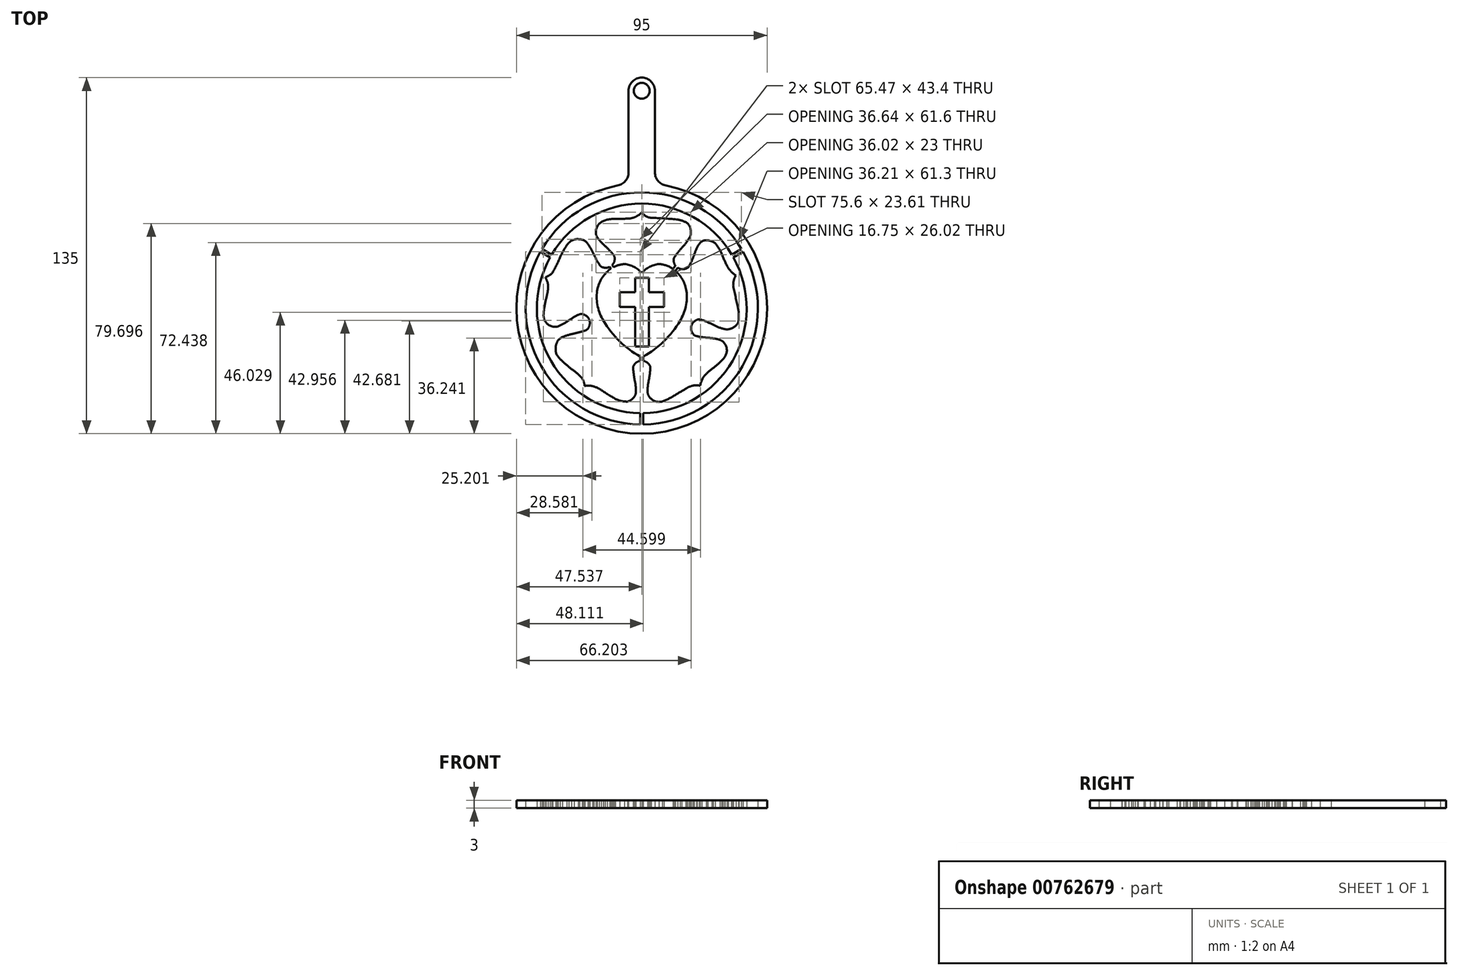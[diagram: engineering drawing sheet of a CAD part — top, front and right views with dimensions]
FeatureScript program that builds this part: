
annotation { "Feature Type Name" : "Feature", "Feature Type Description" : "" }
export const myFeature = defineFeature(function(context is Context, id is Id, definition is map)
    precondition{}
    {
        {
            var Q0;
            Q0=qCreatedBy(makeId("Top.planeOp"),FACE);
            var sketch = newSketch(context, id + "F0", { "sketchPlane" : qUnion([Q0])});
            skLineSegment(sketch, "E0.bottom", {"start": v(-45, 45) * mm, "end": v(45, 45) * mm});
            skLineSegment(sketch, "E0.top", {"start": v(-45, -45) * mm, "end": v(45, -45) * mm});
            skLineSegment(sketch, "E0.left", {"start": v(-45, 45) * mm, "end": v(-45, -45) * mm});
            skLineSegment(sketch, "E0.right", {"start": v(45, 45) * mm, "end": v(45, -45) * mm});
            skCircle(sketch, "E1", {"center": v(0, 0) * mm, "radius": 44 * mm});
            skCircle(sketch, "E2", {"center": v(0, 0) * mm, "radius": 39.75 * mm});
            skLineSegment(sketch, "E3.bottom", {"start": v(-2.5, 11.54) * mm, "end": v(2.7, 11.54) * mm});
            skLineSegment(sketch, "E3.top", {"start": v(-2.5, -14.48) * mm, "end": v(2.7, -14.48) * mm});
            skLineSegment(sketch, "E3.left", {"start": v(-2.5, 11.54) * mm, "end": v(-2.5, -14.48) * mm});
            skLineSegment(sketch, "E3.right", {"start": v(2.7, 11.54) * mm, "end": v(2.7, -14.48) * mm});
            skLineSegment(sketch, "E4.bottom", {"start": v(-8.34, 6.12) * mm, "end": v(8.41, 6.12) * mm});
            skLineSegment(sketch, "E4.top", {"start": v(-8.34, 0.57) * mm, "end": v(8.41, 0.57) * mm});
            skLineSegment(sketch, "E4.left", {"start": v(-8.34, 6.12) * mm, "end": v(-8.34, 0.57) * mm});
            skLineSegment(sketch, "E4.right", {"start": v(8.41, 6.12) * mm, "end": v(8.41, 0.57) * mm});
            skArc(sketch, "E5", {"start": v(6.54, 16.79) * mm, "mid": v(2.95, 15.73) * mm, "end": v(0, 13.44) * mm});
            skArc(sketch, "E6", {"start": v(12, 14.86) * mm, "mid": v(9.4, 16.22) * mm, "end": v(6.54, 16.79) * mm});
            skArc(sketch, "E7", {"start": v(16.95, 6.56) * mm, "mid": v(15.27, 11.18) * mm, "end": v(12, 14.86) * mm});
            skArc(sketch, "E8", {"start": v(14.48, -4.74) * mm, "mid": v(16.7, 0.7) * mm, "end": v(16.95, 6.56) * mm});
            skArc(sketch, "E9", {"start": v(0, -18.58) * mm, "mid": v(8.19, -12.65) * mm, "end": v(14.48, -4.74) * mm});
            skLineSegment(sketch, "E10", {"start": v(0, 13.44) * mm, "end": v(0, -18.58) * mm});
            skArc(sketch, "E11.MirrorCS", {"start": v(-6.54, 16.79) * mm, "mid": v(-2.95, 15.73) * mm, "end": v(0, 13.44) * mm});
            skArc(sketch, "E12.MirrorCS", {"start": v(-12, 14.86) * mm, "mid": v(-9.4, 16.22) * mm, "end": v(-6.54, 16.79) * mm});
            skArc(sketch, "E13.MirrorCS", {"start": v(-16.95, 6.56) * mm, "mid": v(-15.27, 11.18) * mm, "end": v(-12, 14.86) * mm});
            skArc(sketch, "E14.MirrorCS", {"start": v(-14.48, -4.74) * mm, "mid": v(-16.7, 0.7) * mm, "end": v(-16.95, 6.56) * mm});
            skArc(sketch, "E15.MirrorCS", {"start": v(0, -18.58) * mm, "mid": v(-8.19, -12.65) * mm, "end": v(-14.48, -4.74) * mm});
            skArc(sketch, "E16", {"start": v(0, 36.44) * mm, "mid": v(1.55, 35) * mm, "end": v(3.57, 34.33) * mm});
            skArc(sketch, "E17", {"start": v(13.22, 33.72) * mm, "mid": v(8.4, 34.11) * mm, "end": v(3.57, 34.33) * mm});
            skArc(sketch, "E18", {"start": v(18.08, 31.78) * mm, "mid": v(15.79, 33.1) * mm, "end": v(13.22, 33.72) * mm});
            skArc(sketch, "E19", {"start": v(19.53, 28.72) * mm, "mid": v(19.07, 30.38) * mm, "end": v(18.08, 31.78) * mm});
            skArc(sketch, "E20", {"start": v(17.86, 25.1) * mm, "mid": v(18.99, 26.77) * mm, "end": v(19.53, 28.72) * mm});
            skLineSegment(sketch, "E21", {"start": v(17.86, 25.1) * mm, "end": v(15.52, 22.1) * mm});
            skArc(sketch, "E22", {"start": v(15.52, 22.1) * mm, "mid": v(14.15, 20.52) * mm, "end": v(13.15, 18.7) * mm});
            skArc(sketch, "E23", {"start": v(13.15, 18.7) * mm, "mid": v(14.32, 15.74) * mm, "end": v(17.36, 16.66) * mm});
            skArc(sketch, "E24", {"start": v(17.36, 16.66) * mm, "mid": v(18.3, 18.64) * mm, "end": v(19.06, 20.7) * mm});
            skArc(sketch, "E25", {"start": v(20.46, 24.12) * mm, "mid": v(19.7, 22.44) * mm, "end": v(19.06, 20.7) * mm});
            skArc(sketch, "E26", {"start": v(23.5, 26.42) * mm, "mid": v(21.72, 25.62) * mm, "end": v(20.46, 24.12) * mm});
            skArc(sketch, "E27", {"start": v(27.15, 25.4) * mm, "mid": v(25.46, 26.38) * mm, "end": v(23.5, 26.42) * mm});
            skArc(sketch, "E28", {"start": v(30.36, 20.5) * mm, "mid": v(29, 23.12) * mm, "end": v(27.15, 25.4) * mm});
            skArc(sketch, "E29", {"start": v(30.36, 20.5) * mm, "mid": v(31.52, 17.83) * mm, "end": v(32.79, 15.22) * mm});
            skArc(sketch, "E30", {"start": v(32.79, 15.22) * mm, "mid": v(34.12, 13.72) * mm, "end": v(35.67, 12.44) * mm});
            skArc(sketch, "E31", {"start": v(35.67, 12.44) * mm, "mid": v(34.86, 10.6) * mm, "end": v(34.66, 8.59) * mm});
            skArc(sketch, "E32", {"start": v(34.66, 8.59) * mm, "mid": v(35.54, 4.4) * mm, "end": v(36.48, 0.21) * mm});
            skArc(sketch, "E33", {"start": v(36.56, -5.45) * mm, "mid": v(36.8, -2.62) * mm, "end": v(36.48, 0.21) * mm});
            skArc(sketch, "E34", {"start": v(34.01, -8.4) * mm, "mid": v(35.55, -7.15) * mm, "end": v(36.56, -5.45) * mm});
            skArc(sketch, "E35", {"start": v(31.16, -8.48) * mm, "mid": v(32.6, -8.67) * mm, "end": v(34.01, -8.4) * mm});
            skArc(sketch, "E36", {"start": v(24.37, -5.6) * mm, "mid": v(27.72, -7.16) * mm, "end": v(31.16, -8.48) * mm});
            skArc(sketch, "E37", {"start": v(24.37, -5.6) * mm, "mid": v(22.92, -5.17) * mm, "end": v(21.4, -5.26) * mm});
            skArc(sketch, "E38", {"start": v(21.4, -5.26) * mm, "mid": v(20.45, -5.78) * mm, "end": v(19.83, -6.68) * mm});
            skArc(sketch, "E39", {"start": v(19.83, -6.68) * mm, "mid": v(19.7, -7.91) * mm, "end": v(20.32, -8.98) * mm});
            skArc(sketch, "E40", {"start": v(20.32, -8.98) * mm, "mid": v(21.64, -9.79) * mm, "end": v(23.15, -10.1) * mm});
            skArc(sketch, "E41", {"start": v(26.9, -10.46) * mm, "mid": v(25.03, -10.25) * mm, "end": v(23.15, -10.1) * mm});
            skArc(sketch, "E42", {"start": v(30.56, -11.14) * mm, "mid": v(28.76, -10.62) * mm, "end": v(26.9, -10.46) * mm});
            skArc(sketch, "E43", {"start": v(32.8, -13.84) * mm, "mid": v(31.94, -12.28) * mm, "end": v(30.56, -11.14) * mm});
            skArc(sketch, "E44", {"start": v(32.36, -17.04) * mm, "mid": v(32.87, -15.44) * mm, "end": v(32.77, -13.76) * mm});
            skArc(sketch, "E45", {"start": v(30.2, -19.83) * mm, "mid": v(31.4, -18.53) * mm, "end": v(32.36, -17.04) * mm});
            skArc(sketch, "E46", {"start": v(27.09, -22.58) * mm, "mid": v(28.7, -21.26) * mm, "end": v(30.2, -19.83) * mm});
            skArc(sketch, "E47", {"start": v(27.09, -22.58) * mm, "mid": v(25.81, -23.54) * mm, "end": v(24.61, -24.6) * mm});
            skArc(sketch, "E48", {"start": v(24.61, -24.6) * mm, "mid": v(23.02, -26.68) * mm, "end": v(22.2, -29.16) * mm});
            skArc(sketch, "E49", {"start": v(22.2, -29.16) * mm, "mid": v(22.18, -29.26) * mm, "end": v(22.2, -29.36) * mm});
            skArc(sketch, "E50", {"start": v(22.2, -29.36) * mm, "mid": v(20.65, -29.14) * mm, "end": v(19.12, -29.35) * mm});
            skArc(sketch, "E51", {"start": v(19.12, -29.35) * mm, "mid": v(18.01, -29.75) * mm, "end": v(16.98, -30.3) * mm});
            skArc(sketch, "E52", {"start": v(12.71, -32.8) * mm, "mid": v(14.85, -31.56) * mm, "end": v(16.98, -30.3) * mm});
            skArc(sketch, "E53", {"start": v(7.81, -35.27) * mm, "mid": v(10.34, -34.18) * mm, "end": v(12.71, -32.8) * mm});
            skArc(sketch, "E54", {"start": v(1.9, -34.29) * mm, "mid": v(4.72, -35.62) * mm, "end": v(7.81, -35.27) * mm});
            skArc(sketch, "E55", {"start": v(1.07, -30.57) * mm, "mid": v(1.11, -32.52) * mm, "end": v(1.9, -34.29) * mm});
            skArc(sketch, "E56", {"start": v(1.9, -24.2) * mm, "mid": v(1.4, -27.38) * mm, "end": v(1.07, -30.57) * mm});
            skArc(sketch, "E57", {"start": v(1.9, -24.2) * mm, "mid": v(1.96, -22.8) * mm, "end": v(1.75, -21.4) * mm});
            skArc(sketch, "E58", {"start": v(1.75, -21.4) * mm, "mid": v(1.07, -20.51) * mm, "end": v(0, -20.16) * mm});
            skArc(sketch, "E59", {"start": v(0, -20.16) * mm, "mid": v(-1.25, -20.37) * mm, "end": v(-2.16, -21.26) * mm});
            skArc(sketch, "E60", {"start": v(-2.16, -21.26) * mm, "mid": v(-2.56, -22.74) * mm, "end": v(-2.48, -24.28) * mm});
            skArc(sketch, "E61", {"start": v(-1.5, -30.4) * mm, "mid": v(-1.92, -27.33) * mm, "end": v(-2.48, -24.28) * mm});
            skArc(sketch, "E62", {"start": v(-2.8, -34) * mm, "mid": v(-1.78, -32.33) * mm, "end": v(-1.5, -30.4) * mm});
            skArc(sketch, "E63", {"start": v(-5.21, -35.34) * mm, "mid": v(-3.87, -34.92) * mm, "end": v(-2.8, -34) * mm});
            skArc(sketch, "E64", {"start": v(-9.96, -34.34) * mm, "mid": v(-7.65, -35.14) * mm, "end": v(-5.21, -35.34) * mm});
            skArc(sketch, "E65", {"start": v(-15.27, -31.03) * mm, "mid": v(-12.64, -32.73) * mm, "end": v(-9.96, -34.34) * mm});
            skArc(sketch, "E66", {"start": v(-15.27, -31.03) * mm, "mid": v(-16.9, -30.09) * mm, "end": v(-18.68, -29.48) * mm});
            skArc(sketch, "E67", {"start": v(-18.68, -29.48) * mm, "mid": v(-20.16, -29.28) * mm, "end": v(-21.66, -29.42) * mm});
            skArc(sketch, "E68", {"start": v(-21.66, -29.42) * mm, "mid": v(-21.95, -27.92) * mm, "end": v(-22.6, -26.55) * mm});
            skArc(sketch, "E69", {"start": v(-22.6, -26.55) * mm, "mid": v(-24.45, -24.66) * mm, "end": v(-26.57, -23.08) * mm});
            skArc(sketch, "E70", {"start": v(-30, -20.12) * mm, "mid": v(-28.3, -21.62) * mm, "end": v(-26.57, -23.08) * mm});
            skArc(sketch, "E71", {"start": v(-33.13, -16.23) * mm, "mid": v(-31.72, -18.3) * mm, "end": v(-30, -20.12) * mm});
            skArc(sketch, "E72", {"start": v(-33.13, -12.1) * mm, "mid": v(-33.5, -14.16) * mm, "end": v(-33.13, -16.23) * mm});
            skArc(sketch, "E73", {"start": v(-30.28, -9.88) * mm, "mid": v(-31.94, -10.68) * mm, "end": v(-33.13, -12.1) * mm});
            skArc(sketch, "E74", {"start": v(-24.48, -8.35) * mm, "mid": v(-27.4, -9.06) * mm, "end": v(-30.28, -9.88) * mm});
            skArc(sketch, "E75", {"start": v(-24.48, -8.35) * mm, "mid": v(-22.88, -7.92) * mm, "end": v(-21.4, -7.18) * mm});
            skArc(sketch, "E76", {"start": v(-21.4, -7.18) * mm, "mid": v(-20.69, -6) * mm, "end": v(-20.79, -4.62) * mm});
            skArc(sketch, "E77", {"start": v(-20.79, -4.62) * mm, "mid": v(-21.7, -3.47) * mm, "end": v(-23.15, -3.15) * mm});
            skArc(sketch, "E78", {"start": v(-23.15, -3.15) * mm, "mid": v(-25.09, -3.75) * mm, "end": v(-26.83, -4.79) * mm});
            skArc(sketch, "E79", {"start": v(-30.09, -6.9) * mm, "mid": v(-28.44, -5.88) * mm, "end": v(-26.83, -4.79) * mm});
            skArc(sketch, "E80", {"start": v(-33.05, -7.75) * mm, "mid": v(-31.5, -7.58) * mm, "end": v(-30.09, -6.9) * mm});
            skArc(sketch, "E81", {"start": v(-36.25, -6.16) * mm, "mid": v(-34.83, -7.3) * mm, "end": v(-33.05, -7.75) * mm});
            skArc(sketch, "E82", {"start": v(-37.17, -1.77) * mm, "mid": v(-37.1, -4.05) * mm, "end": v(-36.25, -6.16) * mm});
            skArc(sketch, "E83", {"start": v(-36.28, 3.58) * mm, "mid": v(-36.83, 0.92) * mm, "end": v(-37.17, -1.77) * mm});
            skArc(sketch, "E84", {"start": v(-36.28, 3.58) * mm, "mid": v(-35.73, 5.9) * mm, "end": v(-35.5, 8.25) * mm});
            skArc(sketch, "E85", {"start": v(-35.5, 8.25) * mm, "mid": v(-35.77, 10.1) * mm, "end": v(-36.54, 11.8) * mm});
            skArc(sketch, "E86", {"start": v(-36.54, 11.8) * mm, "mid": v(-35.04, 12.53) * mm, "end": v(-33.78, 13.62) * mm});
            skArc(sketch, "E87", {"start": v(-33.78, 13.62) * mm, "mid": v(-32.25, 16.49) * mm, "end": v(-30.92, 19.46) * mm});
            skArc(sketch, "E88", {"start": v(-27.68, 25.02) * mm, "mid": v(-29.42, 22.3) * mm, "end": v(-30.92, 19.46) * mm});
            skArc(sketch, "E89", {"start": v(-23.95, 27.13) * mm, "mid": v(-26.01, 26.42) * mm, "end": v(-27.68, 25.02) * mm});
            skArc(sketch, "E90", {"start": v(-21.49, 26.75) * mm, "mid": v(-22.68, 27.16) * mm, "end": v(-23.95, 27.13) * mm});
            skArc(sketch, "E91", {"start": v(-19.35, 24.34) * mm, "mid": v(-20.3, 25.65) * mm, "end": v(-21.49, 26.75) * mm});
            skArc(sketch, "E92", {"start": v(-16.95, 19.97) * mm, "mid": v(-18.13, 22.17) * mm, "end": v(-19.35, 24.34) * mm});
            skArc(sketch, "E93", {"start": v(-16.95, 19.97) * mm, "mid": v(-16.12, 18.38) * mm, "end": v(-14.94, 17.03) * mm});
            skArc(sketch, "E94", {"start": v(-14.94, 17.03) * mm, "mid": v(-13.5, 16.52) * mm, "end": v(-12.08, 17.12) * mm});
            skArc(sketch, "E95", {"start": v(-12.08, 17.12) * mm, "mid": v(-11.4, 18.14) * mm, "end": v(-11.33, 19.36) * mm});
            skArc(sketch, "E96", {"start": v(-11.33, 19.36) * mm, "mid": v(-11.61, 20.08) * mm, "end": v(-12.02, 20.74) * mm});
            skArc(sketch, "E97", {"start": v(-12.02, 20.74) * mm, "mid": v(-13.03, 21.91) * mm, "end": v(-14.14, 22.98) * mm});
            skArc(sketch, "E98", {"start": v(-16.39, 24.95) * mm, "mid": v(-15.27, 23.96) * mm, "end": v(-14.14, 22.98) * mm});
            skArc(sketch, "E99", {"start": v(-18.17, 27.59) * mm, "mid": v(-17.42, 26.17) * mm, "end": v(-16.39, 24.95) * mm});
            skArc(sketch, "E100", {"start": v(-18.06, 30.68) * mm, "mid": v(-18.41, 29.15) * mm, "end": v(-18.17, 27.59) * mm});
            skArc(sketch, "E101", {"start": v(-15.51, 32.97) * mm, "mid": v(-17.01, 32.08) * mm, "end": v(-18.06, 30.68) * mm});
            skArc(sketch, "E102", {"start": v(-10.83, 33.93) * mm, "mid": v(-13.2, 33.62) * mm, "end": v(-15.51, 32.97) * mm});
            skArc(sketch, "E103", {"start": v(-10.83, 33.93) * mm, "mid": v(-8.11, 33.96) * mm, "end": v(-5.4, 34.03) * mm});
            skArc(sketch, "E104", {"start": v(-5.4, 34.03) * mm, "mid": v(-3.95, 34.19) * mm, "end": v(-2.56, 34.61) * mm});
            skArc(sketch, "E105", {"start": v(-2.56, 34.61) * mm, "mid": v(-1.17, 35.37) * mm, "end": v(0, 36.44) * mm});
            skCircle(sketch, "E106", {"center": v(0, 0) * mm, "radius": 47.5 * mm});
            skLineSegment(sketch, "E107", {"start": v(0.6, -44) * mm, "end": v(0.6, -39.75) * mm});
            skLineSegment(sketch, "E108.MirrorCS", {"start": v(-0.6, -44) * mm, "end": v(-0.6, -39.75) * mm});
            skLineSegment(sketch, "E109.1.0", {"start": v(38.4, 21.48) * mm, "end": v(34.72, 19.35) * mm});
            skLineSegment(sketch, "E109.1.1", {"start": v(37.8, 22.52) * mm, "end": v(34.12, 20.4) * mm});
            skLineSegment(sketch, "E109.2.0", {"start": v(-37.8, 22.52) * mm, "end": v(-34.12, 20.4) * mm});
            skLineSegment(sketch, "E109.2.1", {"start": v(-38.4, 21.48) * mm, "end": v(-34.72, 19.35) * mm});
            skLineSegment(sketch, "E110", {"start": v(0.6, -20.27) * mm, "end": v(0.6, -18.26) * mm});
            skLineSegment(sketch, "E111.MirrorCS", {"start": v(-0.6, -20.27) * mm, "end": v(-0.6, -18.26) * mm});
            skLineSegment(sketch, "E112.2.0", {"start": v(14.1, 15.86) * mm, "end": v(12.74, 14.25) * mm});
            skLineSegment(sketch, "E112.2.1", {"start": v(13.27, 16.75) * mm, "end": v(11.8, 15) * mm});
            skLineSegment(sketch, "E112.anchor1", {"start": v(0, 0) * mm, "end": v(-0.6, -20.27) * mm, "construction": true});
            skLineSegment(sketch, "E112.anchor2", {"start": v(0, 0) * mm, "end": v(13.49, 15.14) * mm, "construction": true});
            skLineSegment(sketch, "E113.2.0", {"start": v(-11.86, 17.34) * mm, "end": v(-10.66, 15.69) * mm});
            skLineSegment(sketch, "E113.2.1", {"start": v(-12.84, 16.65) * mm, "end": v(-11.7, 15.07) * mm});
            skLineSegment(sketch, "E113.anchor2", {"start": v(0, 0) * mm, "end": v(-11.43, 16.75) * mm, "construction": true});
            skPoint(sketch, "E114.orphan", {"position": v(-12.4, 16.05) * mm});
            skPoint(sketch, "E115.orphan", {"position": v(12.57, 15.91) * mm});
            skPoint(sketch, "E116.orphan", {"position": v(11.27, 14.37) * mm});
            skPoint(sketch, "E117.orphan", {"position": v(12.2, 13.6) * mm});
            skPoint(sketch, "E118.orphan", {"position": v(-11.22, 14.42) * mm});
            skPoint(sketch, "E119.orphan", {"position": v(-10.24, 15.12) * mm});
            skLineSegment(sketch, "E120.top", {"start": v(-5, 87.5) * mm, "end": v(5, 87.5) * mm});
            skLineSegment(sketch, "E120.left", {"start": v(-5, 47.24) * mm, "end": v(-5, 87.5) * mm});
            skLineSegment(sketch, "E120.right", {"start": v(5, 47.24) * mm, "end": v(5, 87.5) * mm});
            skArc(sketch, "E121", {"start": v(3.1, -33.84) * mm, "mid": v(5.23, -35.28) * mm, "end": v(7.81, -35.27) * mm});
            skArc(sketch, "E122", {"start": v(2.2, -31.7) * mm, "mid": v(2.47, -32.84) * mm, "end": v(3.1, -33.84) * mm});
            skArc(sketch, "E123", {"start": v(2.7, -27.1) * mm, "mid": v(2.3, -29.39) * mm, "end": v(2.2, -31.7) * mm});
            skArc(sketch, "E124", {"start": v(2.7, -27.1) * mm, "mid": v(3.03, -25.04) * mm, "end": v(3.24, -22.97) * mm});
            skArc(sketch, "E125", {"start": v(3.24, -22.97) * mm, "mid": v(3.16, -21.96) * mm, "end": v(2.63, -21.1) * mm});
            skArc(sketch, "E126.MirrorCS", {"start": v(-3.1, -33.84) * mm, "mid": v(-5.23, -35.28) * mm, "end": v(-7.81, -35.27) * mm});
            skArc(sketch, "E127.MirrorCS", {"start": v(-2.2, -31.7) * mm, "mid": v(-2.47, -32.84) * mm, "end": v(-3.1, -33.84) * mm});
            skArc(sketch, "E128.MirrorCS", {"start": v(-2.7, -27.1) * mm, "mid": v(-2.3, -29.39) * mm, "end": v(-2.2, -31.7) * mm});
            skArc(sketch, "E129.MirrorCS", {"start": v(-2.7, -27.1) * mm, "mid": v(-3.03, -25.04) * mm, "end": v(-3.24, -22.97) * mm});
            skArc(sketch, "E130.MirrorCS", {"start": v(-3.24, -22.97) * mm, "mid": v(-3.16, -21.96) * mm, "end": v(-2.63, -21.1) * mm});
            skArc(sketch, "E131", {"start": v(2.63, -21.1) * mm, "mid": v(0, -19.83) * mm, "end": v(-2.63, -21.1) * mm});
            skArc(sketch, "E132.1.1", {"start": v(26.54, -5.96) * mm, "mid": v(28.63, -6.97) * mm, "end": v(30.84, -7.7) * mm});
            skArc(sketch, "E132.1.2", {"start": v(26.54, -5.96) * mm, "mid": v(24.65, -5.09) * mm, "end": v(22.71, -4.32) * mm});
            skArc(sketch, "E132.1.3", {"start": v(22.71, -4.32) * mm, "mid": v(21.72, -4.13) * mm, "end": v(20.75, -4.4) * mm});
            skArc(sketch, "E132.1.4", {"start": v(20.75, -4.4) * mm, "mid": v(18.8, -6.59) * mm, "end": v(19.31, -9.47) * mm});
            skArc(sketch, "E132.1.5", {"start": v(20.95, -10.56) * mm, "mid": v(20, -10.2) * mm, "end": v(19.31, -9.47) * mm});
            skArc(sketch, "E132.1.6", {"start": v(25.06, -11.17) * mm, "mid": v(23, -10.92) * mm, "end": v(20.95, -10.56) * mm});
            skArc(sketch, "E132.1.7", {"start": v(25.06, -11.17) * mm, "mid": v(27.37, -11.41) * mm, "end": v(29.64, -11.94) * mm});
            skArc(sketch, "E132.1.8", {"start": v(29.64, -11.94) * mm, "mid": v(30.66, -12.51) * mm, "end": v(31.44, -13.38) * mm});
            skArc(sketch, "E132.1.9", {"start": v(31.44, -13.38) * mm, "mid": v(32.25, -15.83) * mm, "end": v(31.54, -18.31) * mm});
            skArc(sketch, "E132.2.1", {"start": v(15.15, 22.94) * mm, "mid": v(16.67, 24.7) * mm, "end": v(17.96, 26.62) * mm});
            skArc(sketch, "E132.2.2", {"start": v(15.15, 22.94) * mm, "mid": v(13.8, 21.34) * mm, "end": v(12.56, 19.67) * mm});
            skArc(sketch, "E132.2.3", {"start": v(12.56, 19.67) * mm, "mid": v(12.11, 18.77) * mm, "end": v(12.12, 17.76) * mm});
            skArc(sketch, "E132.2.4", {"start": v(12.12, 17.76) * mm, "mid": v(13.73, 15.31) * mm, "end": v(16.64, 15.05) * mm});
            skArc(sketch, "E132.2.5", {"start": v(18.12, 16.33) * mm, "mid": v(17.53, 15.51) * mm, "end": v(16.64, 15.05) * mm});
            skArc(sketch, "E132.2.6", {"start": v(19.79, 20.15) * mm, "mid": v(19, 18.22) * mm, "end": v(18.12, 16.33) * mm});
            skArc(sketch, "E132.2.7", {"start": v(19.79, 20.15) * mm, "mid": v(20.63, 22.31) * mm, "end": v(21.73, 24.36) * mm});
            skArc(sketch, "E132.3.1", {"start": v(-18.12, 20.33) * mm, "mid": v(-19.14, 22.42) * mm, "end": v(-20.41, 24.36) * mm});
            skArc(sketch, "E132.3.2", {"start": v(-18.12, 20.33) * mm, "mid": v(-17.17, 18.48) * mm, "end": v(-16.12, 16.68) * mm});
            skArc(sketch, "E132.3.3", {"start": v(-16.12, 16.68) * mm, "mid": v(-15.47, 15.9) * mm, "end": v(-14.53, 15.52) * mm});
            skArc(sketch, "E132.3.4", {"start": v(-14.53, 15.52) * mm, "mid": v(-11.66, 16.04) * mm, "end": v(-10.27, 18.62) * mm});
            skArc(sketch, "E132.3.5", {"start": v(-10.88, 20.49) * mm, "mid": v(-10.35, 19.63) * mm, "end": v(-10.27, 18.62) * mm});
            skArc(sketch, "E132.3.6", {"start": v(-13.74, 23.51) * mm, "mid": v(-12.26, 22.04) * mm, "end": v(-10.88, 20.49) * mm});
            skArc(sketch, "E132.3.7", {"start": v(-13.74, 23.51) * mm, "mid": v(-15.4, 25.13) * mm, "end": v(-16.86, 26.94) * mm});
            skArc(sketch, "E132.3.8", {"start": v(-16.86, 26.94) * mm, "mid": v(-17.3, 28.03) * mm, "end": v(-17.39, 29.2) * mm});
            skArc(sketch, "E132.3.9", {"start": v(-17.39, 29.2) * mm, "mid": v(-16.5, 31.62) * mm, "end": v(-14.41, 33.13) * mm});
            skArc(sketch, "E132.4.1", {"start": v(-25.57, -9.54) * mm, "mid": v(-27.83, -10.07) * mm, "end": v(-30.01, -10.87) * mm});
            skArc(sketch, "E132.4.2", {"start": v(-25.57, -9.54) * mm, "mid": v(-23.55, -9.04) * mm, "end": v(-21.56, -8.42) * mm});
            skArc(sketch, "E132.4.3", {"start": v(-21.56, -8.42) * mm, "mid": v(-20.66, -7.95) * mm, "end": v(-20.08, -7.13) * mm});
            skArc(sketch, "E132.4.4", {"start": v(-20.08, -7.13) * mm, "mid": v(-19.93, -4.21) * mm, "end": v(-22.13, -2.29) * mm});
            skArc(sketch, "E132.4.5", {"start": v(-24.1, -2.46) * mm, "mid": v(-23.13, -2.13) * mm, "end": v(-22.13, -2.29) * mm});
            skArc(sketch, "E132.4.6", {"start": v(-27.68, -4.56) * mm, "mid": v(-25.92, -3.46) * mm, "end": v(-24.1, -2.46) * mm});
            skArc(sketch, "E132.4.7", {"start": v(-27.68, -4.56) * mm, "mid": v(-29.63, -5.82) * mm, "end": v(-31.73, -6.83) * mm});
            skArc(sketch, "E132.4.8", {"start": v(-31.73, -6.83) * mm, "mid": v(-32.88, -7.02) * mm, "end": v(-34.04, -6.84) * mm});
            skArc(sketch, "E132.4.9", {"start": v(-34.04, -6.84) * mm, "mid": v(-36.2, -5.43) * mm, "end": v(-37.2, -3.05) * mm});
            skLineSegment(sketch, "E133", {"start": v(31.54, -18.31) * mm, "end": v(31.5, -18.41) * mm});
            skArc(sketch, "E134", {"start": v(30.84, -7.7) * mm, "mid": v(32.39, -7.94) * mm, "end": v(33.92, -7.63) * mm});
            skArc(sketch, "E135", {"start": v(33.92, -7.63) * mm, "mid": v(35.48, -6.7) * mm, "end": v(36.6, -5.27) * mm});
            skArc(sketch, "E136", {"start": v(17.96, 26.62) * mm, "mid": v(18.53, 27.82) * mm, "end": v(18.58, 29.14) * mm});
            skArc(sketch, "E137", {"start": v(18.58, 29.14) * mm, "mid": v(18.27, 30.87) * mm, "end": v(17.3, 32.33) * mm});
            skArc(sketch, "E138", {"start": v(24.37, 25.83) * mm, "mid": v(22.85, 25.45) * mm, "end": v(21.73, 24.36) * mm});
            skArc(sketch, "E139", {"start": v(27.88, 24.61) * mm, "mid": v(26.24, 25.54) * mm, "end": v(24.37, 25.83) * mm});
            skLineSegment(sketch, "E140", {"start": v(-14.41, 33.13) * mm, "end": v(-13.07, 33.64) * mm});
            skArc(sketch, "E141", {"start": v(-20.41, 24.36) * mm, "mid": v(-21.72, 25.7) * mm, "end": v(-23.52, 26.18) * mm});
            skArc(sketch, "E142", {"start": v(-23.52, 26.18) * mm, "mid": v(-26.28, 25.85) * mm, "end": v(-28.36, 24.01) * mm});
            skLineSegment(sketch, "E143", {"start": v(-37.2, -3.05) * mm, "end": v(-37.24, -2.71) * mm});
            skArc(sketch, "E144", {"start": v(-30.01, -10.87) * mm, "mid": v(-31.38, -11.78) * mm, "end": v(-32.26, -13.15) * mm});
            skArc(sketch, "E145", {"start": v(-32.26, -13.15) * mm, "mid": v(-32.63, -15.38) * mm, "end": v(-32.26, -17.6) * mm});
            skSolve(sketch);
        }
        {
            var Q0;
            Q0=makeQuery(id+"F0.imprint","IMPRINT",FACE,{"disambiguationData":[TD([[makeQuery(id+"F0.imprint","IMPRINT",EDGE,{"derivedFrom":sQuery(id+"F0.wireOp",EDGE,"E2")}),1.0]])]});
            var Q1;
            {var subQ0=sQuery(id+"F0.wireOp",EDGE,"jIWKUOGv-LtLH-rBLy-ceK5-i20kqldYji2q");Q1=makeQuery(id+"F0.imprint","IMPRINT",FACE,{"disambiguationData":[TD([[makeQuery(id+"F0.imprint","IMPRINT",EDGE,{"derivedFrom":subQ0}),-1.0]])]});}
            var Q2;
            Q2=makeQuery(id+"F0.imprint","IMPRINT",FACE,{"disambiguationData":[TD([[makeQuery(id+"F0.imprint","IMPRINT",EDGE,{"derivedFrom":sQuery(id+"F0.wireOp",EDGE,"YiZZbCw6-dnjT-kj3F-cHf3-YuvEgeyhBXGH")}),-1.0]])]});
            var Q3;
            {var subQ7=sQuery(id+"F0.wireOp",EDGE,"E106");var subQ8=sQuery(id+"F0.wireOp",EDGE,"E0.bottom");var subQ9=makeQuery(id+"F0.imprint","INTERSECT",VERTEX,{"disambiguationData":[OD(0.0)],"derivedFrom":[subQ8,subQ7]});Q3=makeQuery(id+"F0.imprint","IMPRINT",FACE,{"disambiguationData":[TD([[makeQuery(id+"F0.imprint","IMPRINT",EDGE,{"disambiguationData":[TD([[subQ9,-1.0]])],"derivedFrom":subQ8}),-1.0]])]});}
            var Q4;
            {var subQ0=sQuery(id+"F0.wireOp",EDGE,"E106");var subQ1=sQuery(id+"F0.wireOp",EDGE,"E0.left");var subQ2=makeQuery(id+"F0.imprint","INTERSECT",VERTEX,{"disambiguationData":[OD(0.0)],"derivedFrom":[subQ1,subQ0]});Q4=makeQuery(id+"F0.imprint","IMPRINT",FACE,{"disambiguationData":[TD([[makeQuery(id+"F0.imprint","IMPRINT",EDGE,{"disambiguationData":[TD([[subQ2,-1.0]])],"derivedFrom":subQ1}),-1.0]])]});}
            var Q5;
            {var subQ0=sQuery(id+"F0.wireOp",EDGE,"E106");var subQ1=sQuery(id+"F0.wireOp",EDGE,"E0.right");var subQ2=makeQuery(id+"F0.imprint","INTERSECT",VERTEX,{"disambiguationData":[OD(0.0)],"derivedFrom":[subQ1,subQ0]});Q5=makeQuery(id+"F0.imprint","IMPRINT",FACE,{"disambiguationData":[TD([[makeQuery(id+"F0.imprint","IMPRINT",EDGE,{"disambiguationData":[TD([[subQ2,-1.0]])],"derivedFrom":subQ1}),1.0]])]});}
            var Q6;
            {var subQ0=sQuery(id+"F0.wireOp",EDGE,"E106");var subQ1=sQuery(id+"F0.wireOp",EDGE,"E0.bottom");var subQ2=makeQuery(id+"F0.imprint","INTERSECT",VERTEX,{"disambiguationData":[OD(0.0)],"derivedFrom":[subQ1,subQ0]});Q6=makeQuery(id+"F0.imprint","IMPRINT",FACE,{"disambiguationData":[TD([[makeQuery(id+"F0.imprint","IMPRINT",EDGE,{"disambiguationData":[TD([[subQ2,-1.0]])],"derivedFrom":subQ1}),1.0]])]});}
            var Q7;
            {var subQ0=sQuery(id+"F0.wireOp",EDGE,"E106");var subQ1=sQuery(id+"F0.wireOp",EDGE,"E0.top");var subQ2=makeQuery(id+"F0.imprint","INTERSECT",VERTEX,{"disambiguationData":[OD(0.0)],"derivedFrom":[subQ1,subQ0]});Q7=makeQuery(id+"F0.imprint","IMPRINT",FACE,{"disambiguationData":[TD([[makeQuery(id+"F0.imprint","IMPRINT",EDGE,{"disambiguationData":[TD([[subQ2,-1.0]])],"derivedFrom":subQ1}),-1.0]])]});}
            var Q8;
            {var subQ0=sQuery(id+"F0.wireOp",EDGE,"E107");Q8=makeQuery(id+"F0.imprint","IMPRINT",FACE,{"disambiguationData":[TD([[makeQuery(id+"F0.imprint","IMPRINT",EDGE,{"derivedFrom":subQ0}),1.0]])]});}
            var Q9;
            {var subQ0=sQuery(id+"F0.wireOp",EDGE,"E109.1.0");Q9=makeQuery(id+"F0.imprint","IMPRINT",FACE,{"disambiguationData":[TD([[makeQuery(id+"F0.imprint","IMPRINT",EDGE,{"derivedFrom":subQ0}),-1.0]])]});}
            var Q10;
            {var subQ0=sQuery(id+"F0.wireOp",EDGE,"E109.2.0");Q10=makeQuery(id+"F0.imprint","IMPRINT",FACE,{"disambiguationData":[TD([[makeQuery(id+"F0.imprint","IMPRINT",EDGE,{"derivedFrom":subQ0}),-1.0]])]});}
            var Q11;
            {var subQ0=sQuery(id+"F0.wireOp",EDGE,"d4a8e12d-94f6-4b27-b552-e5b7031537aa.2.0");Q11=makeQuery(id+"F0.imprint","IMPRINT",FACE,{"disambiguationData":[TD([[makeQuery(id+"F0.imprint","IMPRINT",EDGE,{"derivedFrom":subQ0}),-1.0]])]});}
            var Q12;
            {var subQ3=sQuery(id+"F0.wireOp",EDGE,"4ycSwYRN-3BKS-BSTy-OybS-pnCQ9d655v4T.left");Q12=makeQuery(id+"F0.imprint","IMPRINT",FACE,{"disambiguationData":[TD([[makeQuery(id+"F0.imprint","IMPRINT",EDGE,{"derivedFrom":subQ3}),1.0]])]});}
            var Q13;
            {var subQ0=sQuery(id+"F0.wireOp",EDGE,"E4.left");Q13=makeQuery(id+"F0.imprint","IMPRINT",FACE,{"disambiguationData":[TD([[makeQuery(id+"F0.imprint","IMPRINT",EDGE,{"derivedFrom":subQ0}),-1.0]])]});}
            var Q14;
            {var subQ5=sQuery(id+"F0.wireOp",EDGE,"E4.right");Q14=makeQuery(id+"F0.imprint","IMPRINT",FACE,{"disambiguationData":[TD([[makeQuery(id+"F0.imprint","IMPRINT",EDGE,{"derivedFrom":subQ5}),1.0]])]});}
            var Q15;
            {var subQ0=sQuery(id+"F0.wireOp",EDGE,"dee9fc12-ce8e-4c59-aba2-5a7ed089e132.2.0");Q15=makeQuery(id+"F0.imprint","IMPRINT",FACE,{"disambiguationData":[TD([[makeQuery(id+"F0.imprint","IMPRINT",EDGE,{"derivedFrom":subQ0}),1.0]])]});}
            var Q16;
            {var subQ0=sQuery(id+"F0.wireOp",EDGE,"E113.2.0");Q16=makeQuery(id+"F0.imprint","IMPRINT",FACE,{"disambiguationData":[TD([[makeQuery(id+"F0.imprint","IMPRINT",EDGE,{"derivedFrom":subQ0}),-1.0]])]});}
            var Q17;
            {var subQ0=sQuery(id+"F0.wireOp",EDGE,"E112.2.0");Q17=makeQuery(id+"F0.imprint","IMPRINT",FACE,{"disambiguationData":[TD([[makeQuery(id+"F0.imprint","IMPRINT",EDGE,{"derivedFrom":subQ0}),-1.0]])]});}
            var Q18;
            {var subQ9=sQuery(id+"F0.wireOp",EDGE,"E110");Q18=makeQuery(id+"F0.imprint","IMPRINT",FACE,{"disambiguationData":[TD([[makeQuery(id+"F0.imprint","IMPRINT",EDGE,{"derivedFrom":subQ9}),1.0]])]});}
            var Q19;
            Q19=makeQuery(id+"F0.imprint","IMPRINT",FACE,{"disambiguationData":[TD([[makeQuery(id+"F0.imprint","IMPRINT",EDGE,{"derivedFrom":sQuery(id+"F0.wireOp",EDGE,"E120.top")}),-1.0]])]});
            var Q20;
            {var subQ5=sQuery(id+"F0.wireOp",EDGE,"E60");Q20=makeQuery(id+"F0.imprint","IMPRINT",FACE,{"disambiguationData":[TD([[makeQuery(id+"F0.imprint","IMPRINT",EDGE,{"derivedFrom":subQ5}),-1.0]])]});}
            var Q21;
            Q21=makeQuery(id+"F0.imprint","IMPRINT",FACE,{"disambiguationData":[TD([[makeQuery(id+"F0.imprint","IMPRINT",EDGE,{"derivedFrom":sQuery(id+"F0.wireOp",EDGE,"E54")}),1.0]])]});
            var Q22;
            {var subQ3=sQuery(id+"F0.wireOp",EDGE,"E96");Q22=makeQuery(id+"F0.imprint","IMPRINT",FACE,{"disambiguationData":[TD([[makeQuery(id+"F0.imprint","IMPRINT",EDGE,{"derivedFrom":subQ3}),-1.0]])]});}
            var Q23;
            {var subQ4=sQuery(id+"F0.wireOp",EDGE,"E89");Q23=makeQuery(id+"F0.imprint","IMPRINT",FACE,{"disambiguationData":[TD([[makeQuery(id+"F0.imprint","IMPRINT",EDGE,{"derivedFrom":subQ4}),1.0]])]});}
            var Q24;
            {var subQ8=sQuery(id+"F0.wireOp",EDGE,"E19");Q24=makeQuery(id+"F0.imprint","IMPRINT",FACE,{"disambiguationData":[TD([[makeQuery(id+"F0.imprint","IMPRINT",EDGE,{"derivedFrom":subQ8}),1.0]])]});}
            var Q25;
            {var subQ5=sQuery(id+"F0.wireOp",EDGE,"E24");Q25=makeQuery(id+"F0.imprint","IMPRINT",FACE,{"disambiguationData":[TD([[makeQuery(id+"F0.imprint","IMPRINT",EDGE,{"derivedFrom":subQ5}),-1.0]])]});}
            var Q26;
            {var subQ5=sQuery(id+"F0.wireOp",EDGE,"E34");Q26=makeQuery(id+"F0.imprint","IMPRINT",FACE,{"disambiguationData":[TD([[makeQuery(id+"F0.imprint","IMPRINT",EDGE,{"derivedFrom":subQ5}),1.0]])]});}
            var Q27;
            {var subQ1=sQuery(id+"F0.wireOp",EDGE,"E6");var subQ6=sQuery(id+"F0.wireOp",EDGE,"E7");var subQ9=makeQuery(id+"F0.imprint","INTERSECT",VERTEX,{"derivedFrom":[subQ1,subQ6]});Q27=makeQuery(id+"F0.imprint","IMPRINT",FACE,{"disambiguationData":[TD([[makeQuery(id+"F0.imprint","IMPRINT",EDGE,{"disambiguationData":[TD([[subQ9,-1.0]])],"derivedFrom":subQ1}),-1.0]])]});}
            var Q28;
            {var subQ1=sQuery(id+"F0.wireOp",EDGE,"E95");var subQ5=sQuery(id+"F0.wireOp",EDGE,"E94");var subQ6=makeQuery(id+"F0.imprint","INTERSECT",VERTEX,{"derivedFrom":[subQ5,subQ1]});Q28=makeQuery(id+"F0.imprint","IMPRINT",FACE,{"disambiguationData":[TD([[makeQuery(id+"F0.imprint","IMPRINT",EDGE,{"disambiguationData":[TD([[subQ6,1.0]])],"derivedFrom":subQ5}),-1.0]])]});}
            var Q29;
            {var subQ3=sQuery(id+"F0.wireOp",EDGE,"E72");Q29=makeQuery(id+"F0.imprint","IMPRINT",FACE,{"disambiguationData":[TD([[makeQuery(id+"F0.imprint","IMPRINT",EDGE,{"derivedFrom":subQ3}),1.0]])]});}
            extrude(context, id + "F1", {"entities" : qUnion([Q0, Q1, Q2, Q3, Q4, Q5, Q6, Q7, Q8, Q9, Q10, Q11, Q12, Q13, Q14, Q15, Q16, Q17, Q18, Q19, Q20, Q21, Q22, Q23, Q24, Q25, Q26, Q27, Q28, Q29]), "depth" : 3 * mm, "offsetDistance" : 25 * mm});
        }
        {
            var Q0;
            Q0=makeQuery(id+"F1.opExtrude","SWEPT_EDGE",EDGE,{"disambiguationData":[OSD([sQuery(id+"F0.wireOp",EDGE,"E106"),sQuery(id+"F0.wireOp",EDGE,"E120.right")])]});
            var Q1;
            Q1=makeQuery(id+"F1.opExtrude","SWEPT_EDGE",EDGE,{"disambiguationData":[OSD([sQuery(id+"F0.wireOp",EDGE,"E106"),sQuery(id+"F0.wireOp",EDGE,"E120.left")])]});
            var Q2;
            Q2=makeQuery(id+"F1.opExtrude","SWEPT_EDGE",EDGE,{"disambiguationData":[OSD([sQuery(id+"F0.wireOp",EDGE,"E120.top"),sQuery(id+"F0.wireOp",EDGE,"E120.left")])]});
            var Q3;
            Q3=makeQuery(id+"F1.opExtrude","SWEPT_EDGE",EDGE,{"disambiguationData":[OSD([sQuery(id+"F0.wireOp",EDGE,"E120.top"),sQuery(id+"F0.wireOp",EDGE,"E120.right")])]});
            fillet(context, id + "F2", {"entities" : qUnion([Q0, Q1, Q2, Q3]), "radius" : 5 * mm, "tangentPropagation" : true, "allowEdgeOverflow" : false});
        }
        {
            var Q0;
            Q0=makeQuery(id+"F1.opExtrude","CAP_FACE",FACE,{"disambiguationData":[OSD([sQuery(id+"F0.wireOp",EDGE,"E1"),sQuery(id+"F0.wireOp",EDGE,"E2"),sQuery(id+"F0.wireOp",EDGE,"E3.bottom"),sQuery(id+"F0.wireOp",EDGE,"E3.top"),sQuery(id+"F0.wireOp",EDGE,"E3.left"),sQuery(id+"F0.wireOp",EDGE,"E3.right"),sQuery(id+"F0.wireOp",EDGE,"E4.bottom"),sQuery(id+"F0.wireOp",EDGE,"E4.top"),sQuery(id+"F0.wireOp",EDGE,"E4.left"),sQuery(id+"F0.wireOp",EDGE,"E4.right"),sQuery(id+"F0.wireOp",EDGE,"E5"),sQuery(id+"F0.wireOp",EDGE,"E6"),sQuery(id+"F0.wireOp",EDGE,"E7"),sQuery(id+"F0.wireOp",EDGE,"E8"),sQuery(id+"F0.wireOp",EDGE,"E9"),sQuery(id+"F0.wireOp",EDGE,"E11.MirrorCS"),sQuery(id+"F0.wireOp",EDGE,"E12.MirrorCS"),sQuery(id+"F0.wireOp",EDGE,"E13.MirrorCS"),sQuery(id+"F0.wireOp",EDGE,"E14.MirrorCS"),sQuery(id+"F0.wireOp",EDGE,"E15.MirrorCS"),sQuery(id+"F0.wireOp",EDGE,"E16"),sQuery(id+"F0.wireOp",EDGE,"E17"),sQuery(id+"F0.wireOp",EDGE,"E18"),sQuery(id+"F0.wireOp",EDGE,"E19"),sQuery(id+"F0.wireOp",EDGE,"E20"),sQuery(id+"F0.wireOp",EDGE,"E21"),sQuery(id+"F0.wireOp",EDGE,"E22"),sQuery(id+"F0.wireOp",EDGE,"E23"),sQuery(id+"F0.wireOp",EDGE,"E24"),sQuery(id+"F0.wireOp",EDGE,"E25"),sQuery(id+"F0.wireOp",EDGE,"E26"),sQuery(id+"F0.wireOp",EDGE,"E27"),sQuery(id+"F0.wireOp",EDGE,"E28"),sQuery(id+"F0.wireOp",EDGE,"E29"),sQuery(id+"F0.wireOp",EDGE,"E30"),sQuery(id+"F0.wireOp",EDGE,"E31"),sQuery(id+"F0.wireOp",EDGE,"E32"),sQuery(id+"F0.wireOp",EDGE,"E33"),sQuery(id+"F0.wireOp",EDGE,"E34"),sQuery(id+"F0.wireOp",EDGE,"E35"),sQuery(id+"F0.wireOp",EDGE,"E36"),sQuery(id+"F0.wireOp",EDGE,"E37"),sQuery(id+"F0.wireOp",EDGE,"E38"),sQuery(id+"F0.wireOp",EDGE,"E39"),sQuery(id+"F0.wireOp",EDGE,"E40"),sQuery(id+"F0.wireOp",EDGE,"E41"),sQuery(id+"F0.wireOp",EDGE,"E42"),sQuery(id+"F0.wireOp",EDGE,"E43"),sQuery(id+"F0.wireOp",EDGE,"E44"),sQuery(id+"F0.wireOp",EDGE,"E45"),sQuery(id+"F0.wireOp",EDGE,"E46"),sQuery(id+"F0.wireOp",EDGE,"E47"),sQuery(id+"F0.wireOp",EDGE,"E48"),sQuery(id+"F0.wireOp",EDGE,"E49"),sQuery(id+"F0.wireOp",EDGE,"E50"),sQuery(id+"F0.wireOp",EDGE,"E51"),sQuery(id+"F0.wireOp",EDGE,"E52"),sQuery(id+"F0.wireOp",EDGE,"E53"),sQuery(id+"F0.wireOp",EDGE,"E54"),sQuery(id+"F0.wireOp",EDGE,"E55"),sQuery(id+"F0.wireOp",EDGE,"E56"),sQuery(id+"F0.wireOp",EDGE,"E57"),sQuery(id+"F0.wireOp",EDGE,"E58"),sQuery(id+"F0.wireOp",EDGE,"E59"),sQuery(id+"F0.wireOp",EDGE,"E60"),sQuery(id+"F0.wireOp",EDGE,"E61"),sQuery(id+"F0.wireOp",EDGE,"E62"),sQuery(id+"F0.wireOp",EDGE,"E63"),sQuery(id+"F0.wireOp",EDGE,"E64"),sQuery(id+"F0.wireOp",EDGE,"E65"),sQuery(id+"F0.wireOp",EDGE,"E66"),sQuery(id+"F0.wireOp",EDGE,"E67"),sQuery(id+"F0.wireOp",EDGE,"E68"),sQuery(id+"F0.wireOp",EDGE,"E69"),sQuery(id+"F0.wireOp",EDGE,"E70"),sQuery(id+"F0.wireOp",EDGE,"E71"),sQuery(id+"F0.wireOp",EDGE,"E72"),sQuery(id+"F0.wireOp",EDGE,"E73"),sQuery(id+"F0.wireOp",EDGE,"E74"),sQuery(id+"F0.wireOp",EDGE,"E75"),sQuery(id+"F0.wireOp",EDGE,"E76"),sQuery(id+"F0.wireOp",EDGE,"E77"),sQuery(id+"F0.wireOp",EDGE,"E78"),sQuery(id+"F0.wireOp",EDGE,"E79"),sQuery(id+"F0.wireOp",EDGE,"E80"),sQuery(id+"F0.wireOp",EDGE,"E81"),sQuery(id+"F0.wireOp",EDGE,"E82"),sQuery(id+"F0.wireOp",EDGE,"E83"),sQuery(id+"F0.wireOp",EDGE,"E84"),sQuery(id+"F0.wireOp",EDGE,"E85"),sQuery(id+"F0.wireOp",EDGE,"E86"),sQuery(id+"F0.wireOp",EDGE,"E87"),sQuery(id+"F0.wireOp",EDGE,"E88"),sQuery(id+"F0.wireOp",EDGE,"E89"),sQuery(id+"F0.wireOp",EDGE,"E90"),sQuery(id+"F0.wireOp",EDGE,"E91"),sQuery(id+"F0.wireOp",EDGE,"E92"),sQuery(id+"F0.wireOp",EDGE,"E93"),sQuery(id+"F0.wireOp",EDGE,"E94"),sQuery(id+"F0.wireOp",EDGE,"E95"),sQuery(id+"F0.wireOp",EDGE,"E96"),sQuery(id+"F0.wireOp",EDGE,"E97"),sQuery(id+"F0.wireOp",EDGE,"E98"),sQuery(id+"F0.wireOp",EDGE,"E99"),sQuery(id+"F0.wireOp",EDGE,"E100"),sQuery(id+"F0.wireOp",EDGE,"E101"),sQuery(id+"F0.wireOp",EDGE,"E102"),sQuery(id+"F0.wireOp",EDGE,"E103"),sQuery(id+"F0.wireOp",EDGE,"E104"),sQuery(id+"F0.wireOp",EDGE,"E105"),sQuery(id+"F0.wireOp",EDGE,"E106"),sQuery(id+"F0.wireOp",EDGE,"E107"),sQuery(id+"F0.wireOp",EDGE,"E108.MirrorCS"),sQuery(id+"F0.wireOp",EDGE,"E109.1.0"),sQuery(id+"F0.wireOp",EDGE,"E109.1.1"),sQuery(id+"F0.wireOp",EDGE,"E109.2.0"),sQuery(id+"F0.wireOp",EDGE,"E109.2.1"),sQuery(id+"F0.wireOp",EDGE,"E110"),sQuery(id+"F0.wireOp",EDGE,"E111.MirrorCS"),sQuery(id+"F0.wireOp",EDGE,"E112.2.0"),sQuery(id+"F0.wireOp",EDGE,"E112.2.1"),sQuery(id+"F0.wireOp",EDGE,"E113.2.0"),sQuery(id+"F0.wireOp",EDGE,"E113.2.1"),sQuery(id+"F0.wireOp",EDGE,"E120.top"),sQuery(id+"F0.wireOp",EDGE,"E120.left"),sQuery(id+"F0.wireOp",EDGE,"E120.right")])],"isStart":false});
            var sketch = newSketch(context, id + "F3", { "sketchPlane" : qUnion([Q0])});
            skCircle(sketch, "E146", {"center": v(0, 82.5) * mm, "radius": 3 * mm});
            skSolve(sketch);
        }
        {
            var Q0;
            Q0 = qSketchRegion(id + "F3", true);
            extrude(context, id + "F4", {"entities" : qUnion([Q0]), "operationType" : NewBodyOperationType.REMOVE, "endBound" : BoundingType.THROUGH_ALL, "oppositeDirection" : true, "depth" : 25 * mm, "offsetDistance" : 25 * mm});
        }
    });
